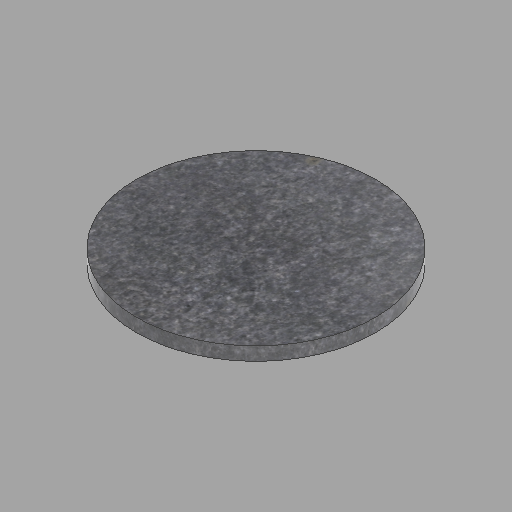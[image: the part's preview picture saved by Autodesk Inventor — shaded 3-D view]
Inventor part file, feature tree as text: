
AUTODESK INVENTOR PART (.ipt)
format: ipt  version: 2023 (Build 270158000, 158)  size: 221,696 bytes
history: native  units: in
note: dims shown in document units (in); Inventor stores cm internally (conversion verified against a paired STEP export)
features: extrude x2, sketch x2, other x1, projected_geometry x1
ambient origin geometry x8: Origin, YZ Plane, XZ Plane, XY Plane, X Axis, Y Axis, Z Axis, Center Point
bodies: Solid1 (feature_tree)
feature tree (6):
  other  "2x36x36-1"
  extrude  "Extrusion1"  Depth=36.0in
  extrude  "Extrusion2"  TaperAngle=0.0deg  [1 undecoded]
  sketch  "Sketch1"  dims[d0=2.0in d1=36.0in]
  sketch  "Sketch2"  dims[d2=36.0in d3=0.0in d4=0.0in d5=0.0in]
  projected_geometry  "Projected Loop1"
note: 1 required parameter value undecoded (feature->parameter linkage not recoverable at this tier; creation-order binding heuristic only, values carry confidence <= 0.55)
